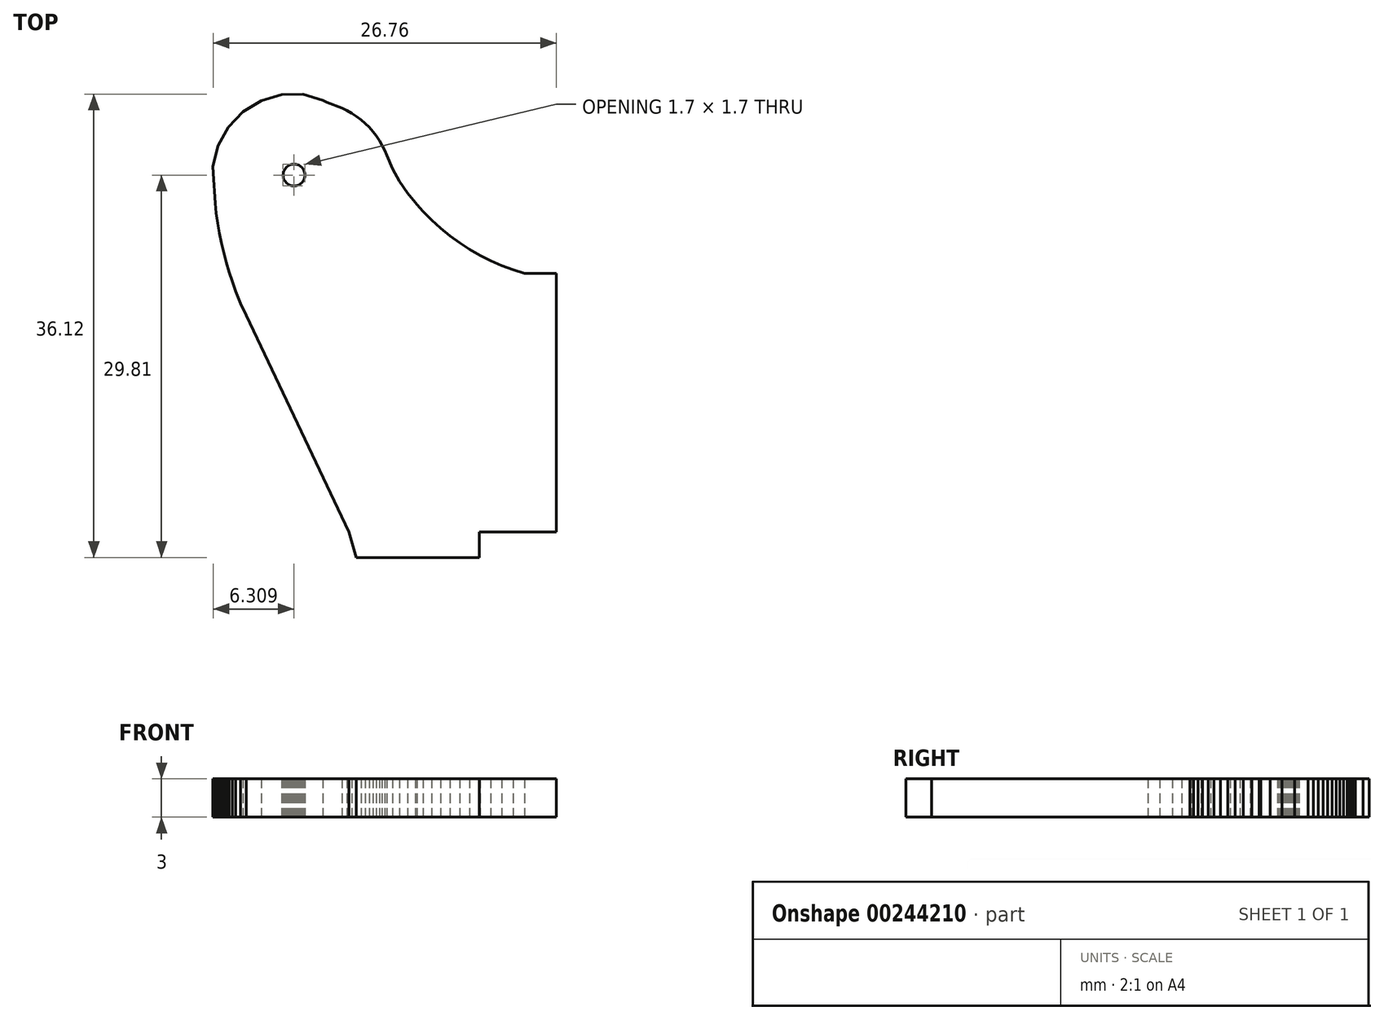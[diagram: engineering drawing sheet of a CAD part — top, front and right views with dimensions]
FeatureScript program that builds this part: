
annotation { "Feature Type Name" : "Feature", "Feature Type Description" : "" }
export const myFeature = defineFeature(function(context is Context, id is Id, definition is map)
    precondition{}
    {
        {
            var Q0;
            Q0=qCreatedBy(makeId("Top.planeOp"),FACE);
            var sketch = newSketch(context, id + "F0", { "sketchPlane" : qUnion([Q0])});
            skLineSegment(sketch, "E0", {"start": v(-11.23, 1.75) * mm, "end": v(-11.72, 2.73) * mm});
            skLineSegment(sketch, "E1", {"start": v(3.3, 8.67) * mm, "end": v(2.51, 9.47) * mm});
            skLineSegment(sketch, "E2", {"start": v(-2.94, 16.78) * mm, "end": v(-2.55, 16.6) * mm});
            skLineSegment(sketch, "E3", {"start": v(-6.23, 11.86) * mm, "end": v(-6.22, 11.75) * mm});
            skLineSegment(sketch, "E4", {"start": v(-6.22, 11.75) * mm, "end": v(-6.23, 11.64) * mm});
            skLineSegment(sketch, "E5", {"start": v(-6.23, 11.64) * mm, "end": v(-6.25, 11.54) * mm});
            skLineSegment(sketch, "E6", {"start": v(-6.25, 11.54) * mm, "end": v(-6.28, 11.44) * mm});
            skLineSegment(sketch, "E7", {"start": v(-6.28, 11.44) * mm, "end": v(-6.33, 11.34) * mm});
            skLineSegment(sketch, "E8", {"start": v(-6.33, 11.34) * mm, "end": v(-6.38, 11.25) * mm});
            skLineSegment(sketch, "E9", {"start": v(-6.38, 11.25) * mm, "end": v(-6.45, 11.17) * mm});
            skLineSegment(sketch, "E10", {"start": v(-6.45, 11.17) * mm, "end": v(-6.53, 11.1) * mm});
            skLineSegment(sketch, "E11", {"start": v(-6.53, 11.1) * mm, "end": v(-6.62, 11.03) * mm});
            skLineSegment(sketch, "E12", {"start": v(-6.62, 11.03) * mm, "end": v(-6.7, 10.98) * mm});
            skLineSegment(sketch, "E13", {"start": v(-6.7, 10.98) * mm, "end": v(-6.8, 10.94) * mm});
            skLineSegment(sketch, "E14", {"start": v(-6.8, 10.94) * mm, "end": v(-6.91, 10.92) * mm});
            skLineSegment(sketch, "E15", {"start": v(-6.91, 10.92) * mm, "end": v(-7.02, 10.9) * mm});
            skLineSegment(sketch, "E16", {"start": v(-7.02, 10.9) * mm, "end": v(-7.12, 10.9) * mm});
            skLineSegment(sketch, "E17", {"start": v(-7.12, 10.9) * mm, "end": v(-7.23, 10.92) * mm});
            skLineSegment(sketch, "E18", {"start": v(-7.23, 10.92) * mm, "end": v(-7.33, 10.94) * mm});
            skLineSegment(sketch, "E19", {"start": v(-7.33, 10.94) * mm, "end": v(-7.43, 10.98) * mm});
            skLineSegment(sketch, "E20", {"start": v(-7.43, 10.98) * mm, "end": v(-7.53, 11.03) * mm});
            skLineSegment(sketch, "E21", {"start": v(-7.53, 11.03) * mm, "end": v(-7.61, 11.1) * mm});
            skLineSegment(sketch, "E22", {"start": v(-7.61, 11.1) * mm, "end": v(-7.7, 11.17) * mm});
            skLineSegment(sketch, "E23", {"start": v(-7.7, 11.17) * mm, "end": v(-7.76, 11.25) * mm});
            skLineSegment(sketch, "E24", {"start": v(-7.76, 11.25) * mm, "end": v(-7.82, 11.34) * mm});
            skLineSegment(sketch, "E25", {"start": v(-7.82, 11.34) * mm, "end": v(-7.86, 11.44) * mm});
            skLineSegment(sketch, "E26", {"start": v(-7.86, 11.44) * mm, "end": v(-7.9, 11.54) * mm});
            skLineSegment(sketch, "E27", {"start": v(-7.9, 11.54) * mm, "end": v(-7.91, 11.64) * mm});
            skLineSegment(sketch, "E28", {"start": v(-7.91, 11.64) * mm, "end": v(-7.92, 11.75) * mm});
            skLineSegment(sketch, "E29", {"start": v(-7.92, 11.75) * mm, "end": v(-7.91, 11.86) * mm});
            skLineSegment(sketch, "E30", {"start": v(-7.91, 11.86) * mm, "end": v(-7.9, 11.96) * mm});
            skLineSegment(sketch, "E31", {"start": v(-7.9, 11.96) * mm, "end": v(-7.86, 12.06) * mm});
            skLineSegment(sketch, "E32", {"start": v(-7.86, 12.06) * mm, "end": v(-7.82, 12.16) * mm});
            skLineSegment(sketch, "E33", {"start": v(-7.82, 12.16) * mm, "end": v(-7.76, 12.25) * mm});
            skLineSegment(sketch, "E34", {"start": v(-7.76, 12.25) * mm, "end": v(-7.7, 12.33) * mm});
            skLineSegment(sketch, "E35", {"start": v(-7.7, 12.33) * mm, "end": v(-7.61, 12.4) * mm});
            skLineSegment(sketch, "E36", {"start": v(-7.61, 12.4) * mm, "end": v(-7.53, 12.47) * mm});
            skLineSegment(sketch, "E37", {"start": v(-7.53, 12.47) * mm, "end": v(-7.43, 12.52) * mm});
            skLineSegment(sketch, "E38", {"start": v(-7.43, 12.52) * mm, "end": v(-7.33, 12.56) * mm});
            skLineSegment(sketch, "E39", {"start": v(-7.33, 12.56) * mm, "end": v(-7.23, 12.59) * mm});
            skLineSegment(sketch, "E40", {"start": v(-7.23, 12.59) * mm, "end": v(-7.12, 12.6) * mm});
            skLineSegment(sketch, "E41", {"start": v(-7.12, 12.6) * mm, "end": v(-7.02, 12.6) * mm});
            skLineSegment(sketch, "E42", {"start": v(-7.02, 12.6) * mm, "end": v(-6.91, 12.59) * mm});
            skLineSegment(sketch, "E43", {"start": v(-6.91, 12.59) * mm, "end": v(-6.8, 12.56) * mm});
            skLineSegment(sketch, "E44", {"start": v(-6.8, 12.56) * mm, "end": v(-6.7, 12.52) * mm});
            skLineSegment(sketch, "E45", {"start": v(-6.7, 12.52) * mm, "end": v(-6.62, 12.47) * mm});
            skLineSegment(sketch, "E46", {"start": v(-6.62, 12.47) * mm, "end": v(-6.53, 12.4) * mm});
            skLineSegment(sketch, "E47", {"start": v(-6.53, 12.4) * mm, "end": v(-6.45, 12.33) * mm});
            skLineSegment(sketch, "E48", {"start": v(-6.45, 12.33) * mm, "end": v(-6.38, 12.25) * mm});
            skLineSegment(sketch, "E49", {"start": v(-6.38, 12.25) * mm, "end": v(-6.33, 12.16) * mm});
            skLineSegment(sketch, "E50", {"start": v(-6.33, 12.16) * mm, "end": v(-6.28, 12.06) * mm});
            skLineSegment(sketch, "E51", {"start": v(-6.28, 12.06) * mm, "end": v(-6.25, 11.96) * mm});
            skLineSegment(sketch, "E52", {"start": v(-6.25, 11.96) * mm, "end": v(-6.23, 11.86) * mm});
            skLineSegment(sketch, "E53", {"start": v(2.37, 9.6) * mm, "end": v(2.51, 9.47) * mm});
            skLineSegment(sketch, "E54", {"start": v(2.51, 9.47) * mm, "end": v(3, 8.9) * mm});
            skLineSegment(sketch, "E55", {"start": v(3, 8.9) * mm, "end": v(3.65, 8.24) * mm});
            skLineSegment(sketch, "E56", {"start": v(3.65, 8.24) * mm, "end": v(4.35, 7.61) * mm});
            skLineSegment(sketch, "E57", {"start": v(4.35, 7.61) * mm, "end": v(5.07, 7.02) * mm});
            skLineSegment(sketch, "E58", {"start": v(5.07, 7.02) * mm, "end": v(5.83, 6.47) * mm});
            skLineSegment(sketch, "E59", {"start": v(5.83, 6.47) * mm, "end": v(6.62, 5.97) * mm});
            skLineSegment(sketch, "E60", {"start": v(6.62, 5.97) * mm, "end": v(7.43, 5.5) * mm});
            skLineSegment(sketch, "E61", {"start": v(7.43, 5.5) * mm, "end": v(8.26, 5.08) * mm});
            skLineSegment(sketch, "E62", {"start": v(8.26, 5.08) * mm, "end": v(9.12, 4.7) * mm});
            skLineSegment(sketch, "E63", {"start": v(9.12, 4.7) * mm, "end": v(10, 4.38) * mm});
            skLineSegment(sketch, "E64", {"start": v(10, 4.38) * mm, "end": v(10.89, 4.1) * mm});
            skLineSegment(sketch, "E65", {"start": v(10.89, 4.1) * mm, "end": v(11.38, 4.1) * mm});
            skLineSegment(sketch, "E66", {"start": v(11.38, 4.1) * mm, "end": v(13.38, 4.1) * mm});
            skLineSegment(sketch, "E67", {"start": v(13.38, 4.1) * mm, "end": v(13.38, -16.06) * mm});
            skLineSegment(sketch, "E68", {"start": v(13.38, -16.06) * mm, "end": v(7.38, -16.06) * mm});
            skLineSegment(sketch, "E69", {"start": v(7.38, -16.06) * mm, "end": v(7.38, -18.06) * mm});
            skLineSegment(sketch, "E70", {"start": v(7.38, -18.06) * mm, "end": v(-2.2, -18.06) * mm});
            skLineSegment(sketch, "E71", {"start": v(-2.2, -18.06) * mm, "end": v(-2.79, -16.06) * mm});
            skLineSegment(sketch, "E72", {"start": v(-2.79, -16.06) * mm, "end": v(-10.8, 0.8) * mm});
            skLineSegment(sketch, "E73", {"start": v(-10.8, 0.8) * mm, "end": v(-11.23, 1.75) * mm});
            skLineSegment(sketch, "E74", {"start": v(-11.23, 1.75) * mm, "end": v(-11.62, 2.7) * mm});
            skLineSegment(sketch, "E75", {"start": v(-11.62, 2.7) * mm, "end": v(-11.88, 3.44) * mm});
            skLineSegment(sketch, "E76", {"start": v(-11.88, 3.44) * mm, "end": v(-12.12, 4.19) * mm});
            skLineSegment(sketch, "E77", {"start": v(-12.12, 4.19) * mm, "end": v(-12.34, 4.94) * mm});
            skLineSegment(sketch, "E78", {"start": v(-12.34, 4.94) * mm, "end": v(-12.54, 5.7) * mm});
            skLineSegment(sketch, "E79", {"start": v(-12.54, 5.7) * mm, "end": v(-12.72, 6.46) * mm});
            skLineSegment(sketch, "E80", {"start": v(-12.72, 6.46) * mm, "end": v(-12.88, 7.23) * mm});
            skLineSegment(sketch, "E81", {"start": v(-12.88, 7.23) * mm, "end": v(-13.01, 8) * mm});
            skLineSegment(sketch, "E82", {"start": v(-13.01, 8) * mm, "end": v(-13.13, 8.77) * mm});
            skLineSegment(sketch, "E83", {"start": v(-13.13, 8.77) * mm, "end": v(-13.22, 9.55) * mm});
            skLineSegment(sketch, "E84", {"start": v(-13.22, 9.55) * mm, "end": v(-13.37, 11.9) * mm});
            skLineSegment(sketch, "E85", {"start": v(-13.37, 11.9) * mm, "end": v(-13.38, 12.44) * mm});
            skLineSegment(sketch, "E86", {"start": v(-13.38, 12.44) * mm, "end": v(-13, 14.05) * mm});
            skLineSegment(sketch, "E87", {"start": v(-13, 14.05) * mm, "end": v(-12.2, 15.5) * mm});
            skLineSegment(sketch, "E88", {"start": v(-12.2, 15.5) * mm, "end": v(-11.05, 16.7) * mm});
            skLineSegment(sketch, "E89", {"start": v(-11.05, 16.7) * mm, "end": v(-9.63, 17.56) * mm});
            skLineSegment(sketch, "E90", {"start": v(-9.63, 17.56) * mm, "end": v(-8.04, 18.03) * mm});
            skLineSegment(sketch, "E91", {"start": v(-8.04, 18.03) * mm, "end": v(-6.38, 18.06) * mm});
            skLineSegment(sketch, "E92", {"start": v(-6.38, 18.06) * mm, "end": v(-4.84, 17.57) * mm});
            skLineSegment(sketch, "E93", {"start": v(-4.84, 17.57) * mm, "end": v(-4.5, 17.43) * mm});
            skLineSegment(sketch, "E94", {"start": v(-4.5, 17.43) * mm, "end": v(-3.33, 16.97) * mm});
            skLineSegment(sketch, "E95", {"start": v(-3.33, 16.97) * mm, "end": v(-2.94, 16.78) * mm});
            skLineSegment(sketch, "E96", {"start": v(-2.94, 16.78) * mm, "end": v(-2.56, 16.56) * mm});
            skLineSegment(sketch, "E97", {"start": v(-2.56, 16.56) * mm, "end": v(-2.2, 16.33) * mm});
            skLineSegment(sketch, "E98", {"start": v(-2.2, 16.33) * mm, "end": v(-1.85, 16.06) * mm});
            skLineSegment(sketch, "E99", {"start": v(-1.85, 16.06) * mm, "end": v(-1.53, 15.78) * mm});
            skLineSegment(sketch, "E100", {"start": v(-1.53, 15.78) * mm, "end": v(-1.22, 15.47) * mm});
            skLineSegment(sketch, "E101", {"start": v(-1.22, 15.47) * mm, "end": v(-0.93, 15.15) * mm});
            skLineSegment(sketch, "E102", {"start": v(-0.93, 15.15) * mm, "end": v(-0.67, 14.8) * mm});
            skLineSegment(sketch, "E103", {"start": v(-0.67, 14.8) * mm, "end": v(-0.42, 14.45) * mm});
            skLineSegment(sketch, "E104", {"start": v(-0.42, 14.45) * mm, "end": v(-0.2, 14.08) * mm});
            skLineSegment(sketch, "E105", {"start": v(-0.2, 14.08) * mm, "end": v(-0.01, 13.69) * mm});
            skLineSegment(sketch, "E106", {"start": v(-0.01, 13.69) * mm, "end": v(0.16, 13.29) * mm});
            skLineSegment(sketch, "E107", {"start": v(0.16, 13.29) * mm, "end": v(0.6, 12.26) * mm});
            skLineSegment(sketch, "E108", {"start": v(0.6, 12.26) * mm, "end": v(1.15, 11.27) * mm});
            skLineSegment(sketch, "E109", {"start": v(1.15, 11.27) * mm, "end": v(1.8, 10.34) * mm});
            skLineSegment(sketch, "E110", {"start": v(1.8, 10.34) * mm, "end": v(2.37, 9.6) * mm});
            skLineSegment(sketch, "E111", {"start": v(-6.22, 11.75) * mm, "end": v(-6.23, 11.86) * mm});
            skLineSegment(sketch, "E112", {"start": v(-6.23, 11.86) * mm, "end": v(-6.25, 11.96) * mm});
            skLineSegment(sketch, "E113", {"start": v(-6.25, 11.96) * mm, "end": v(-6.28, 12.06) * mm});
            skLineSegment(sketch, "E114", {"start": v(-6.28, 12.06) * mm, "end": v(-6.33, 12.16) * mm});
            skLineSegment(sketch, "E115", {"start": v(-6.33, 12.16) * mm, "end": v(-6.38, 12.25) * mm});
            skLineSegment(sketch, "E116", {"start": v(-6.38, 12.25) * mm, "end": v(-6.45, 12.33) * mm});
            skLineSegment(sketch, "E117", {"start": v(-6.45, 12.33) * mm, "end": v(-6.53, 12.4) * mm});
            skLineSegment(sketch, "E118", {"start": v(-6.53, 12.4) * mm, "end": v(-6.62, 12.47) * mm});
            skLineSegment(sketch, "E119", {"start": v(-6.62, 12.47) * mm, "end": v(-6.7, 12.52) * mm});
            skLineSegment(sketch, "E120", {"start": v(-6.7, 12.52) * mm, "end": v(-6.8, 12.56) * mm});
            skLineSegment(sketch, "E121", {"start": v(-6.8, 12.56) * mm, "end": v(-6.91, 12.59) * mm});
            skLineSegment(sketch, "E122", {"start": v(-6.91, 12.59) * mm, "end": v(-7.02, 12.6) * mm});
            skLineSegment(sketch, "E123", {"start": v(-7.02, 12.6) * mm, "end": v(-7.12, 12.6) * mm});
            skLineSegment(sketch, "E124", {"start": v(-7.12, 12.6) * mm, "end": v(-7.23, 12.59) * mm});
            skLineSegment(sketch, "E125", {"start": v(-7.23, 12.59) * mm, "end": v(-7.33, 12.56) * mm});
            skLineSegment(sketch, "E126", {"start": v(-7.33, 12.56) * mm, "end": v(-7.43, 12.52) * mm});
            skLineSegment(sketch, "E127", {"start": v(-7.43, 12.52) * mm, "end": v(-7.53, 12.47) * mm});
            skLineSegment(sketch, "E128", {"start": v(-7.53, 12.47) * mm, "end": v(-7.61, 12.4) * mm});
            skLineSegment(sketch, "E129", {"start": v(-7.61, 12.4) * mm, "end": v(-7.7, 12.33) * mm});
            skLineSegment(sketch, "E130", {"start": v(-7.7, 12.33) * mm, "end": v(-7.76, 12.25) * mm});
            skLineSegment(sketch, "E131", {"start": v(-7.76, 12.25) * mm, "end": v(-7.82, 12.16) * mm});
            skLineSegment(sketch, "E132", {"start": v(-7.82, 12.16) * mm, "end": v(-7.86, 12.06) * mm});
            skLineSegment(sketch, "E133", {"start": v(-7.86, 12.06) * mm, "end": v(-7.9, 11.96) * mm});
            skLineSegment(sketch, "E134", {"start": v(-7.9, 11.96) * mm, "end": v(-7.91, 11.86) * mm});
            skLineSegment(sketch, "E135", {"start": v(-7.91, 11.86) * mm, "end": v(-7.92, 11.75) * mm});
            skLineSegment(sketch, "E136", {"start": v(-7.92, 11.75) * mm, "end": v(-7.91, 11.64) * mm});
            skLineSegment(sketch, "E137", {"start": v(-7.91, 11.64) * mm, "end": v(-7.9, 11.54) * mm});
            skLineSegment(sketch, "E138", {"start": v(-7.9, 11.54) * mm, "end": v(-7.86, 11.44) * mm});
            skLineSegment(sketch, "E139", {"start": v(-7.86, 11.44) * mm, "end": v(-7.82, 11.34) * mm});
            skLineSegment(sketch, "E140", {"start": v(-7.82, 11.34) * mm, "end": v(-7.76, 11.25) * mm});
            skLineSegment(sketch, "E141", {"start": v(-7.76, 11.25) * mm, "end": v(-7.7, 11.17) * mm});
            skLineSegment(sketch, "E142", {"start": v(-7.7, 11.17) * mm, "end": v(-7.61, 11.1) * mm});
            skLineSegment(sketch, "E143", {"start": v(-7.61, 11.1) * mm, "end": v(-7.53, 11.03) * mm});
            skLineSegment(sketch, "E144", {"start": v(-7.53, 11.03) * mm, "end": v(-7.43, 10.98) * mm});
            skLineSegment(sketch, "E145", {"start": v(-7.43, 10.98) * mm, "end": v(-7.33, 10.94) * mm});
            skLineSegment(sketch, "E146", {"start": v(-7.33, 10.94) * mm, "end": v(-7.23, 10.92) * mm});
            skLineSegment(sketch, "E147", {"start": v(-7.23, 10.92) * mm, "end": v(-7.12, 10.9) * mm});
            skLineSegment(sketch, "E148", {"start": v(-7.12, 10.9) * mm, "end": v(-7.02, 10.9) * mm});
            skLineSegment(sketch, "E149", {"start": v(-7.02, 10.9) * mm, "end": v(-6.91, 10.92) * mm});
            skLineSegment(sketch, "E150", {"start": v(-6.91, 10.92) * mm, "end": v(-6.8, 10.94) * mm});
            skLineSegment(sketch, "E151", {"start": v(-6.8, 10.94) * mm, "end": v(-6.7, 10.98) * mm});
            skLineSegment(sketch, "E152", {"start": v(-6.7, 10.98) * mm, "end": v(-6.62, 11.03) * mm});
            skLineSegment(sketch, "E153", {"start": v(-6.62, 11.03) * mm, "end": v(-6.53, 11.1) * mm});
            skLineSegment(sketch, "E154", {"start": v(-6.53, 11.1) * mm, "end": v(-6.45, 11.17) * mm});
            skLineSegment(sketch, "E155", {"start": v(-6.45, 11.17) * mm, "end": v(-6.38, 11.25) * mm});
            skLineSegment(sketch, "E156", {"start": v(-6.38, 11.25) * mm, "end": v(-6.33, 11.34) * mm});
            skLineSegment(sketch, "E157", {"start": v(-6.33, 11.34) * mm, "end": v(-6.28, 11.44) * mm});
            skLineSegment(sketch, "E158", {"start": v(-6.28, 11.44) * mm, "end": v(-6.25, 11.54) * mm});
            skLineSegment(sketch, "E159", {"start": v(-6.25, 11.54) * mm, "end": v(-6.23, 11.64) * mm});
            skLineSegment(sketch, "E160", {"start": v(-6.23, 11.64) * mm, "end": v(-6.22, 11.75) * mm});
            skSolve(sketch);
        }
        {
            var Q0;
            Q0 = qSketchRegion(id + "F0", true);
            extrude(context, id + "F1", {"entities" : qUnion([Q0]), "depth" : 3 * mm});
        }
    });
